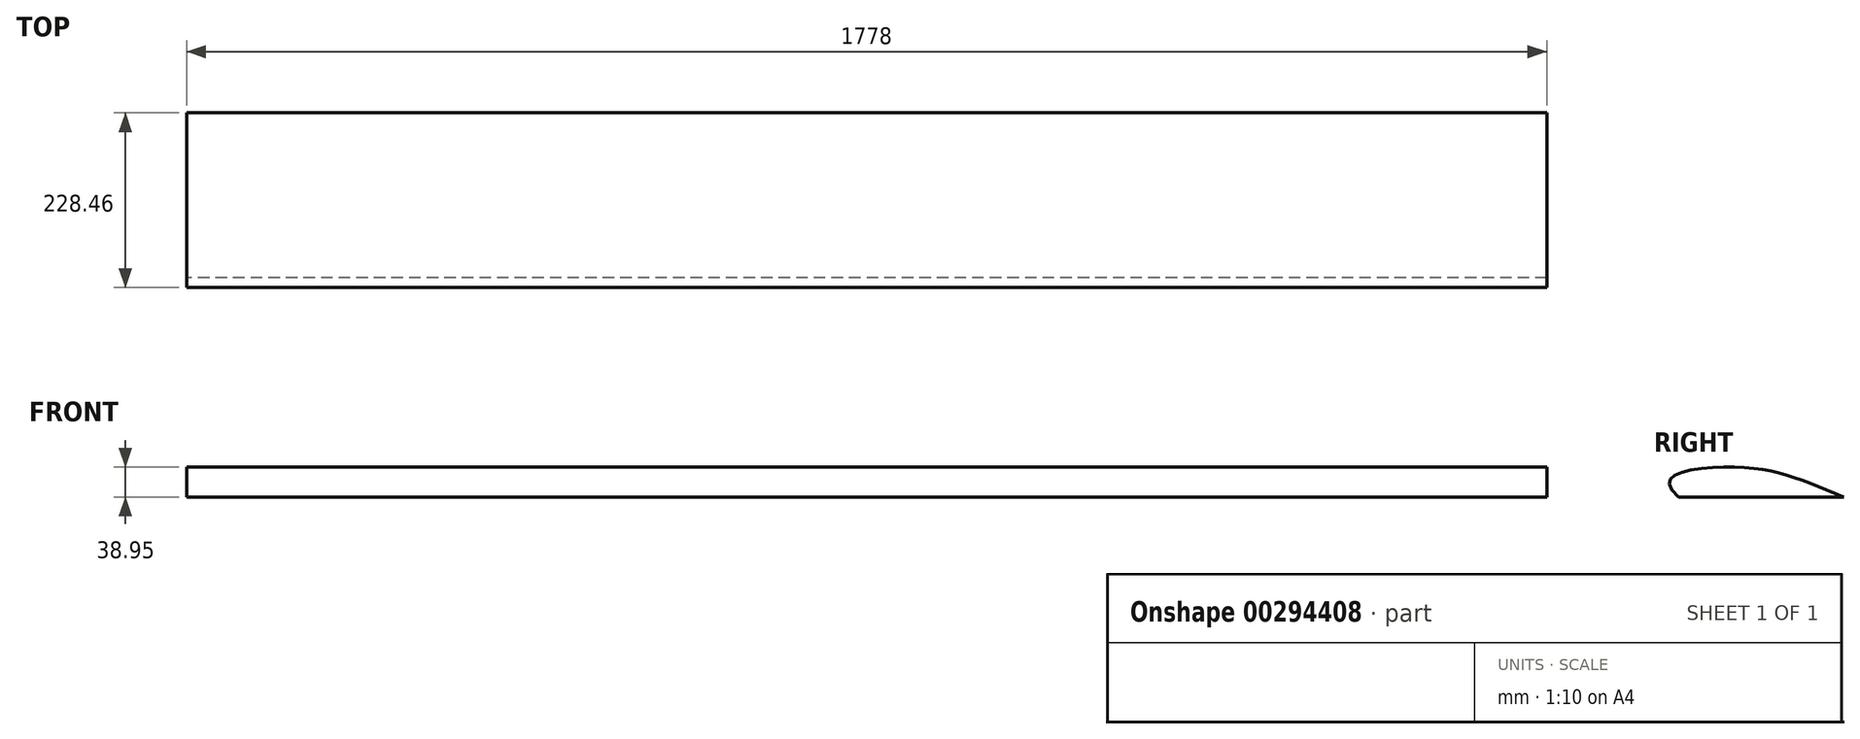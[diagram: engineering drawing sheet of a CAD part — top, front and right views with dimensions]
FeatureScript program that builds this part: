
annotation { "Feature Type Name" : "Feature", "Feature Type Description" : "" }
export const myFeature = defineFeature(function(context is Context, id is Id, definition is map)
    precondition{}
    {
        {
            var Q0;
            Q0=qCreatedBy(makeId("Right.planeOp"),FACE);
            var sketch = newSketch(context, id + "F0", { "sketchPlane" : qUnion([Q0])});
            skLineSegment(sketch, "E0", {"start": v(-215.9, 0) * mm, "end": v(0, 0) * mm});
            skFitSpline(sketch, "E1", {"points": [v(-215.9, 0) * mm, v(-150.55, 38.95) * mm, v(0, 0) * mm], "startDerivative": vector(-283.75, 226.93) * mm, "endDerivative": vector(284.4, -113.5) * mm});
            skSolve(sketch);
        }
        {
            var Q0;
            Q0=makeQuery(id+"F0.imprint","IMPRINT",FACE,{"disambiguationData":[TD([[makeQuery(id+"F0.imprint","IMPRINT",EDGE,{"derivedFrom":sQuery(id+"F0.wireOp",EDGE,"E0")}),1.0]])]});
            extrude(context, id + "F1", {"entities" : qUnion([Q0]), "depth" : 1778 * mm, "offsetDistance" : 25.4 * mm});
        }
    });
